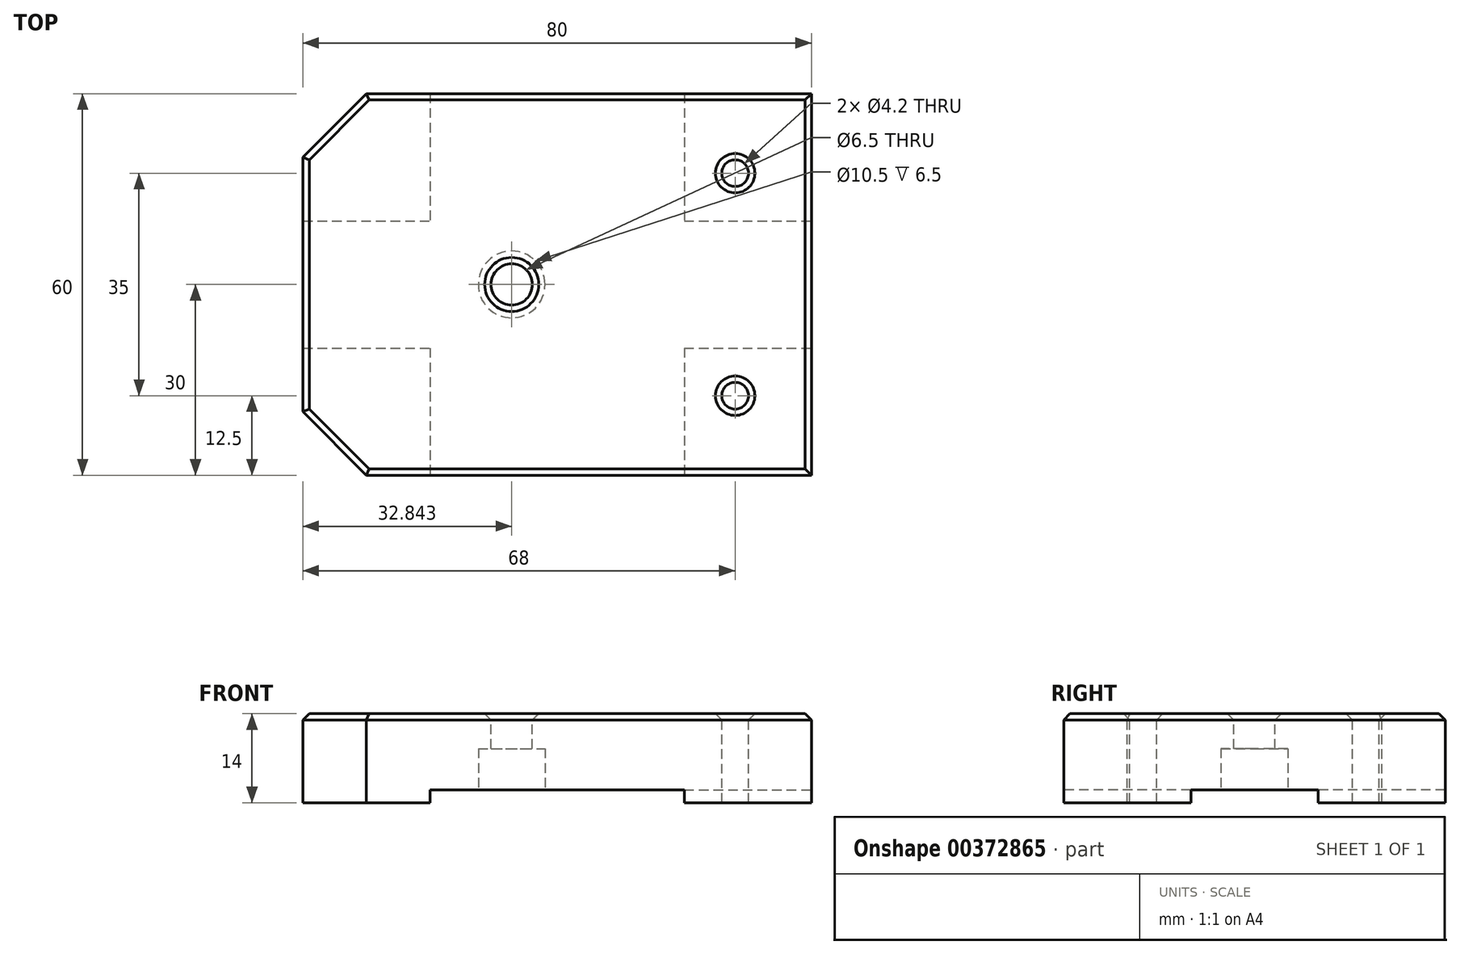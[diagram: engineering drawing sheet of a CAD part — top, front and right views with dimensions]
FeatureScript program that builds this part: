
annotation { "Feature Type Name" : "Feature", "Feature Type Description" : "" }
export const myFeature = defineFeature(function(context is Context, id is Id, definition is map)
    precondition{}
    {
        {
            var Q0;
            Q0=qCreatedBy(makeId("Top.planeOp"),FACE);
            var sketch = newSketch(context, id + "F0", { "sketchPlane" : qUnion([Q0])});
            skLineSegment(sketch, "E0.bottom", {"start": v(-40, -30) * mm, "end": v(40, -30) * mm});
            skLineSegment(sketch, "E0.top", {"start": v(-40, 30) * mm, "end": v(40, 30) * mm});
            skLineSegment(sketch, "E0.left", {"start": v(-40, -30) * mm, "end": v(-40, 30) * mm});
            skLineSegment(sketch, "E0.right", {"start": v(40, -30) * mm, "end": v(40, 30) * mm});
            skPoint(sketch, "E0.middle", {"position": v(0, 0) * mm});
            skSolve(sketch);
        }
        {
            var Q0;
            Q0=makeQuery(id+"F0.imprint","IMPRINT",FACE,{"disambiguationData":[TD([[makeQuery(id+"F0.imprint","IMPRINT",EDGE,{"derivedFrom":sQuery(id+"F0.wireOp",EDGE,"E0.bottom")}),1.0]])]});
            extrude(context, id + "F1", {"entities" : qUnion([Q0]), "depth" : 14 * mm});
        }
        {
            var Q0;
            Q0=makeQuery(id+"F1.opExtrude","CAP_FACE",FACE,{"disambiguationData":[OSD([sQuery(id+"F0.wireOp",EDGE,"E0.bottom"),sQuery(id+"F0.wireOp",EDGE,"E0.top"),sQuery(id+"F0.wireOp",EDGE,"E0.left"),sQuery(id+"F0.wireOp",EDGE,"E0.right")])],"isStart":true});
            var sketch = newSketch(context, id + "F2", { "sketchPlane" : qUnion([Q0])});
            skLineSegment(sketch, "E1.bottom", {"start": v(-50, -10) * mm, "end": v(50, -10) * mm});
            skLineSegment(sketch, "E1.top", {"start": v(-50, 10) * mm, "end": v(50, 10) * mm});
            skLineSegment(sketch, "E1.left", {"start": v(-50, -10) * mm, "end": v(-50, 10) * mm});
            skLineSegment(sketch, "E1.right", {"start": v(50, -10) * mm, "end": v(50, 10) * mm});
            skPoint(sketch, "E1.middle", {"position": v(0, 0) * mm});
            skSolve(sketch);
        }
        {
            var Q0;
            {var subQ0=sQuery(id+"F2.wireOp",EDGE,"E1.bottom");var subQ1=makeQuery(id+"F1.opExtrude","CAP_EDGE",EDGE,{"disambiguationData":[OSD([sQuery(id+"F0.wireOp",EDGE,"E0.left")])],"isStart":true});var subQ2=makeQuery(id+"F2.imprint","INTERSECT",VERTEX,{"derivedFrom":[subQ1,subQ0]});Q0=makeQuery(id+"F2.imprint","IMPRINT",FACE,{"disambiguationData":[TD([[makeQuery(id+"F2.imprint","IMPRINT",EDGE,{"disambiguationData":[TD([[subQ2,-1.0]])],"derivedFrom":subQ0}),1.0]])]});}
            extrude(context, id + "F3", {"entities" : qUnion([Q0]), "operationType" : NewBodyOperationType.REMOVE, "oppositeDirection" : true, "depth" : 2 * mm});
        }
        {
            var Q0;
            {var subQ0=sQuery(id+"F0.wireOp",EDGE,"E0.bottom");var subQ1=sQuery(id+"F0.wireOp",EDGE,"E0.right");var subQ2=sQuery(id+"F0.wireOp",EDGE,"E0.left");Q0=makeQuery(id+"F3.boolean.opBoolean","SPLIT",FACE,{"disambiguationData":[TD([makeQuery(id+"F1.opExtrude","SWEPT_FACE",FACE,{"disambiguationData":[OSD([subQ0])]})])],"derivedFrom":makeQuery(id+"F1.opExtrude","CAP_FACE",FACE,{"disambiguationData":[OSD([subQ0,sQuery(id+"F0.wireOp",EDGE,"E0.top"),subQ2,subQ1])],"isStart":true})});}
            var sketch = newSketch(context, id + "F4", { "sketchPlane" : qUnion([Q0])});
            skLineSegment(sketch, "E2.bottom", {"start": v(-20, -30) * mm, "end": v(20, -30) * mm});
            skLineSegment(sketch, "E2.top", {"start": v(-20, 30) * mm, "end": v(20, 30) * mm});
            skLineSegment(sketch, "E2.left", {"start": v(-20, -30) * mm, "end": v(-20, 30) * mm});
            skLineSegment(sketch, "E2.right", {"start": v(20, -30) * mm, "end": v(20, 30) * mm});
            skPoint(sketch, "E2.middle", {"position": v(0, 0) * mm});
            skSolve(sketch);
        }
        {
            var Q0;
            {var subQ0=sQuery(id+"F4.wireOp",EDGE,"E2.top");Q0=makeQuery(id+"F4.imprint","IMPRINT",FACE,{"disambiguationData":[TD([[makeQuery(id+"F4.imprint","IMPRINT",EDGE,{"derivedFrom":subQ0}),-1.0]])]});}
            var Q1;
            {var subQ0=sQuery(id+"F4.wireOp",EDGE,"E2.bottom");Q1=makeQuery(id+"F4.imprint","IMPRINT",FACE,{"disambiguationData":[TD([[makeQuery(id+"F4.imprint","IMPRINT",EDGE,{"derivedFrom":subQ0}),1.0]])]});}
            extrude(context, id + "F5", {"entities" : qUnion([Q0, Q1]), "operationType" : NewBodyOperationType.REMOVE, "oppositeDirection" : true, "depth" : 2 * mm});
        }
        {
            var Q0;
            Q0=makeQuery(id+"F1.opExtrude","SWEPT_EDGE",EDGE,{"disambiguationData":[OSD([sQuery(id+"F0.wireOp",EDGE,"E0.top"),sQuery(id+"F0.wireOp",EDGE,"E0.left")])]});
            var Q1;
            Q1=makeQuery(id+"F1.opExtrude","SWEPT_EDGE",EDGE,{"disambiguationData":[OSD([sQuery(id+"F0.wireOp",EDGE,"E0.bottom"),sQuery(id+"F0.wireOp",EDGE,"E0.left")])]});
            chamfer(context, id + "F6", {"entities" : qUnion([Q0, Q1]), "width" : 10 * mm, "tangentPropagation" : true});
        }
        {
            var Q0;
            Q0=makeQuery(id+"F1.opExtrude","CAP_FACE",FACE,{"disambiguationData":[OSD([sQuery(id+"F0.wireOp",EDGE,"E0.bottom"),sQuery(id+"F0.wireOp",EDGE,"E0.top"),sQuery(id+"F0.wireOp",EDGE,"E0.left"),sQuery(id+"F0.wireOp",EDGE,"E0.right")])],"isStart":false});
            var sketch = newSketch(context, id + "F7", { "sketchPlane" : qUnion([Q0])});
            skLineSegment(sketch, "E3", {"start": v(-12.33, 0) * mm, "end": v(0, 0) * mm, "construction": true});
            skLineSegment(sketch, "E4", {"start": v(-7.16, 6.62) * mm, "end": v(-7.16, -7.14) * mm, "construction": true});
            skCircle(sketch, "E5", {"center": v(-7.16, 0) * mm, "radius": 3.25 * mm});
            skSolve(sketch);
        }
        {
            var Q0;
            Q0=makeQuery(id+"F7.imprint","IMPRINT",FACE,{"disambiguationData":[TD([[makeQuery(id+"F7.imprint","IMPRINT",EDGE,{"derivedFrom":sQuery(id+"F7.wireOp",EDGE,"E5")}),1.0]])]});
            extrude(context, id + "F8", {"entities" : qUnion([Q0]), "operationType" : NewBodyOperationType.REMOVE, "oppositeDirection" : true, "depth" : 25 * mm});
        }
        {
            var Q0;
            Q0=makeQuery(id+"F5.boolean.opBoolean","MERGE",FACE,{"derivedFrom":[makeQuery(id+"F3.boolean.opBoolean","COPY",FACE,{"derivedFrom":makeQuery(id+"F3.opExtrude","CAP_FACE",FACE,{"disambiguationData":[OSD([sQuery(id+"F0.wireOp",EDGE,"E0.left"),sQuery(id+"F0.wireOp",EDGE,"E0.right"),sQuery(id+"F2.wireOp",EDGE,"E1.bottom"),sQuery(id+"F2.wireOp",EDGE,"E1.top")])],"isStart":false})}),makeQuery(id+"F5.opExtrude","CAP_FACE",FACE,{"disambiguationData":[OSD([sQuery(id+"F4.wireOp",EDGE,"E2.bottom"),sQuery(id+"F4.wireOp",EDGE,"E2.top"),sQuery(id+"F4.wireOp",EDGE,"E2.left"),sQuery(id+"F4.wireOp",EDGE,"E2.right")])],"isStart":false})]});
            var sketch = newSketch(context, id + "F9", { "sketchPlane" : qUnion([Q0])});
            skCircle(sketch, "E6", {"center": v(-7.16, 0) * mm, "radius": 5.25 * mm});
            skSolve(sketch);
        }
        {
            var Q0;
            Q0 = qSketchRegion(id + "F9", true);
            extrude(context, id + "F10", {"entities" : qUnion([Q0]), "operationType" : NewBodyOperationType.REMOVE, "oppositeDirection" : true, "depth" : 6.5 * mm});
        }
        {
            var Q0;
            Q0=makeQuery(id+"F1.opExtrude","CAP_FACE",FACE,{"disambiguationData":[OSD([sQuery(id+"F0.wireOp",EDGE,"E0.bottom"),sQuery(id+"F0.wireOp",EDGE,"E0.top"),sQuery(id+"F0.wireOp",EDGE,"E0.left"),sQuery(id+"F0.wireOp",EDGE,"E0.right")])],"isStart":false});
            var sketch = newSketch(context, id + "F11", { "sketchPlane" : qUnion([Q0])});
            skPoint(sketch, "E7", {"position": v(28, 17.5) * mm});
            skPoint(sketch, "E8", {"position": v(28, -17.5) * mm});
            skSolve(sketch);
        }
        {
            var Q0;
            Q0=sQuery(id+"F11.wireOp",VERTEX,"E7");
            var Q1;
            Q1=sQuery(id+"F11.wireOp",VERTEX,"E8");
            var Q2;
            Q2=makeQuery(id+"F1.opExtrude","SWEPT_BODY",BODY,{"disambiguationData":[OSD([sQuery(id+"F0.wireOp",EDGE,"E0.bottom"),sQuery(id+"F0.wireOp",EDGE,"E0.top"),sQuery(id+"F0.wireOp",EDGE,"E0.left"),sQuery(id+"F0.wireOp",EDGE,"E0.right")])]});
            hole(context, id + "F12", {"style" : HoleStyle.SIMPLE, "endStyle" : HoleEndStyle.THROUGH, "standardTappedOrClearance" : lookupTablePath({ "standard" : "ISO", "engagement" : "75%", "pitch" : "0.8 mm", "size" : "M5", "type" : "Tapped" }), "standardBlindInLast" : lookupTablePath({ "standard" : "ISO", "engagement" : "75%", "pitch" : "0.8 mm", "size" : "M5", "type" : "Tapped" }), "holeDiameter" : 4.2 * mm, "showTappedDepth" : true, "isTappedThrough" : true, "tappedDepth" : 12 * mm, "tapClearance" : 3, "locations" : qUnion([Q0, Q1]), "scope" : qUnion([Q2]), "majorDiameter" : 5 * mm});
        }
        {
            var Q0;
            Q0=makeQuery(id+"F1.opExtrude","CAP_FACE",FACE,{"disambiguationData":[OSD([sQuery(id+"F0.wireOp",EDGE,"E0.bottom"),sQuery(id+"F0.wireOp",EDGE,"E0.top"),sQuery(id+"F0.wireOp",EDGE,"E0.left"),sQuery(id+"F0.wireOp",EDGE,"E0.right")])],"isStart":false});
            chamfer(context, id + "F13", {"entities" : qUnion([Q0]), "width" : 1 * mm, "tangentPropagation" : true});
        }
    });
